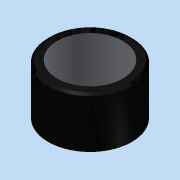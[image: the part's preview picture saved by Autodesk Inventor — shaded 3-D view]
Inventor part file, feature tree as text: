
AUTODESK INVENTOR PART (.ipt)
format: ipt  version: 2015 (Build 190159000, 159)  size: 982,016 bytes
history: native  units: in
note: dims shown in document units (in); Inventor stores cm internally (conversion verified against a paired STEP export)
features: other x6, extrude x2, sketch x2, move_body x1, projected_geometry x1
ambient origin geometry x8: Origin, YZ Plane, XZ Plane, XY Plane, X Axis, Y Axis, Z Axis, Center Point
bodies: Solid1 (feature_tree), Solid2 (feature_tree)
feature tree (12):
  other  "Wheel.ipt"
  other  "RingGear.ipt"
  extrude  "Extrusion1"  Depth=0.3937in
  move_body  "Move Body1"
  extrude  "Extrusion2"  TaperAngle=0.0deg  [1 undecoded]
  other  "Solid1::Wheel.ipt"
  other  "TaggingFeature1"
  sketch  "Sketch1"  dims[d0=0.3937in]
  other  "Solid1::RingGear.ipt"
  other  "TaggingFeature2"
  sketch  "Sketch2"  dims[d2=0.38in d4=0.44in d6=0.815in d7=0.29in d9=1.025in d10=0.2898in d11=0.36in d13=1.14in d14=0.834in d15=0.0in d17=0.865in d18=0.1in d19=0.296in d20=0.0in d21=0.15in d23=0.0in d24=0.168in d25=0.18in d27=0.05in d28=2.3622in d29=360.0deg d31=0.168in d32=0.18in d34=30.0deg d35=0.09in d36=0.06in d38=0.0in d39=0.05in d40=0.02in d41=2.3622in d42=360.0deg d44=0.08in d47=0.08in d48=0.292in d1=2.5591in d3=0.0in d5=0.0in d8=0.3937in d12=90.0deg d16=0.0in d22=0.0in]
  projected_geometry  "Project Cut Edges1"
note: 1 required parameter value undecoded (feature->parameter linkage not recoverable at this tier; creation-order binding heuristic only, values carry confidence <= 0.55)
